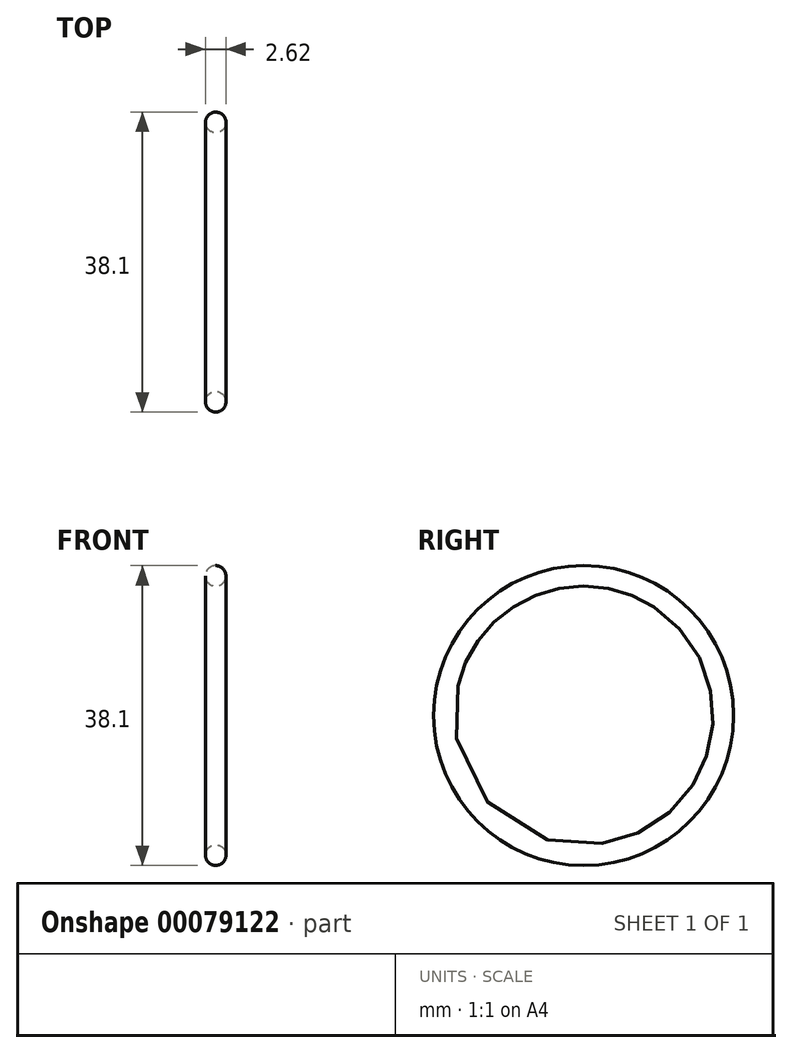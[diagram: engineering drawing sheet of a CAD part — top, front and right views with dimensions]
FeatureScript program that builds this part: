
annotation { "Feature Type Name" : "Feature", "Feature Type Description" : "" }
export const myFeature = defineFeature(function(context is Context, id is Id, definition is map)
    precondition{}
    {
        {
            var Q0;
            Q0=qCreatedBy(makeId("Front.planeOp"),FACE);
            var sketch = newSketch(context, id + "F0", { "sketchPlane" : qUnion([Q0])});
            skLineSegment(sketch, "E0", {"start": v(-14.93, 0) * mm, "end": v(23.62, 0) * mm});
            skCircle(sketch, "E1", {"center": v(6.88, 17.74) * mm, "radius": 1.3 * mm});
            skSolve(sketch);
        }
        {
            var Q0;
            Q0 = qSketchRegion(id + "F0", true);
            var Q1;
            Q1=sQuery(id+"F0.wireOp",EDGE,"E0");
            revolve(context, id + "F1", {"entities" : qUnion([Q0]), "axis" : qUnion([Q1]), "revolveType" : RevolveType.FULL});
        }
    });
